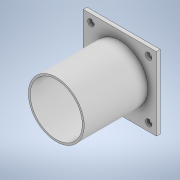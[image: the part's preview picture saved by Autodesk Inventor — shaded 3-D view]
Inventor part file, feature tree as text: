
AUTODESK INVENTOR PART (.ipt)
format: ipt  version: 2022.2 (Build 262287030, 287C)  size: 141,824 bytes
history: native  units: in
note: dims shown in document units (in); Inventor stores cm internally (conversion verified against a paired STEP export)
features: extrude x2, hole x1, sketch x1, projected_geometry x1
ambient origin geometry x8: Origin, YZ Plane, XZ Plane, XY Plane, X Axis, Y Axis, Z Axis, Center Point
bodies: Solid1 (feature_tree)
feature tree (5):
  extrude  "Extrusion1"  Depth=1.4961in
  extrude  "Extrusion2"  Depth=0.3937in
  hole  "Hole1"  [1 undecoded]
  sketch  "Sketch3"  dims[d0=1.4961in d1=1.4961in d2=0.8661in d3=0.8661in d4=0.0787in d5=0.0in d6=1.0236in d7=1.0236in d8=0.9055in d9=1.2992in d10=0.0in d11=0.5906in d12=0.5906in d13=0.7874in d15=1.1811in d16=0.7874in d18=1.1811in d21=0.1339in d22=0.2362in d23=0.1476in d24=0.0984in d25=90.0deg d26=0.3937in d27=0.8108in d28=1.063in d29=1.1417in d30=1.063in]
  projected_geometry  "Project Cut Edges1"
note: 1 required parameter value undecoded (feature->parameter linkage not recoverable at this tier; creation-order binding heuristic only, values carry confidence <= 0.55)
